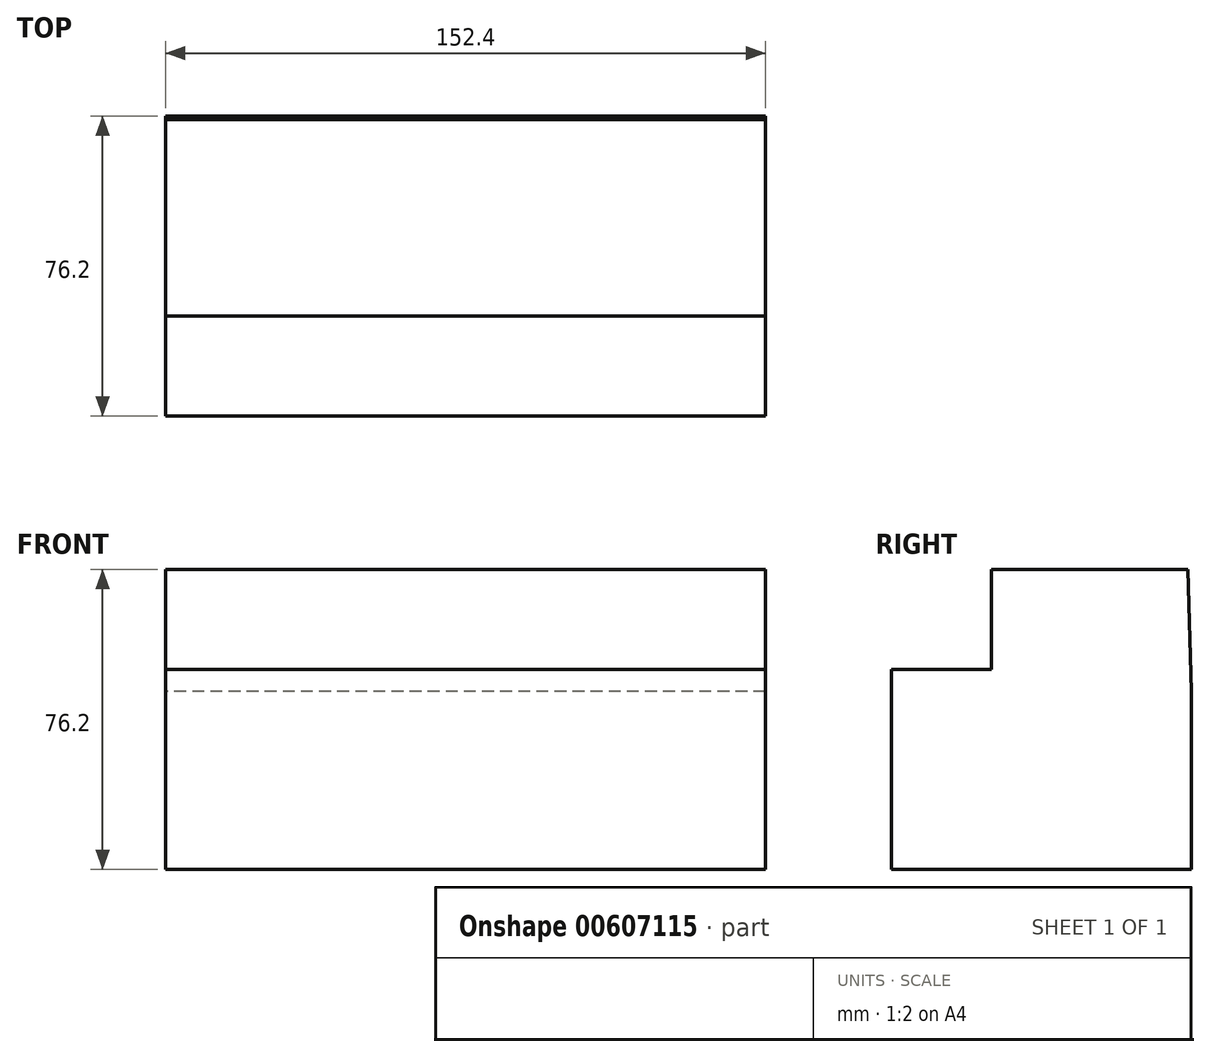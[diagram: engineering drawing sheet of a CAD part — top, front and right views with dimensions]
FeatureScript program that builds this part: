
annotation { "Feature Type Name" : "Feature", "Feature Type Description" : "" }
export const myFeature = defineFeature(function(context is Context, id is Id, definition is map)
    precondition{}
    {
        {
            var Q0;
            Q0=qCreatedBy(makeId("Right.planeOp"),FACE);
            var sketch = newSketch(context, id + "F0", { "sketchPlane" : qUnion([Q0])});
            skLineSegment(sketch, "E0", {"start": v(0, 0) * mm, "end": v(76.2, 0) * mm});
            skLineSegment(sketch, "E1", {"start": v(76.2, 0) * mm, "end": v(76.2, 42.98) * mm});
            skLineSegment(sketch, "E2", {"start": v(0, 0) * mm, "end": v(0, 50.8) * mm});
            skLineSegment(sketch, "E3", {"start": v(0, 50.8) * mm, "end": v(25.4, 50.8) * mm});
            skLineSegment(sketch, "E4", {"start": v(25.4, 50.8) * mm, "end": v(25.4, 76.2) * mm});
            skLineSegment(sketch, "E5", {"start": v(25.4, 76.2) * mm, "end": v(75.33, 76.2) * mm});
            skLineSegment(sketch, "E6", {"start": v(75.33, 76.2) * mm, "end": v(76.2, 45.25) * mm});
            skLineSegment(sketch, "E7", {"start": v(76.2, 45.25) * mm, "end": v(76.2, 42.98) * mm});
            skSolve(sketch);
        }
        {
            var Q0;
            Q0 = qSketchRegion(id + "F0", true);
            extrude(context, id + "F1", {"entities" : qUnion([Q0]), "depth" : 152.4 * mm, "offsetDistance" : 25.4 * mm});
        }
    });
